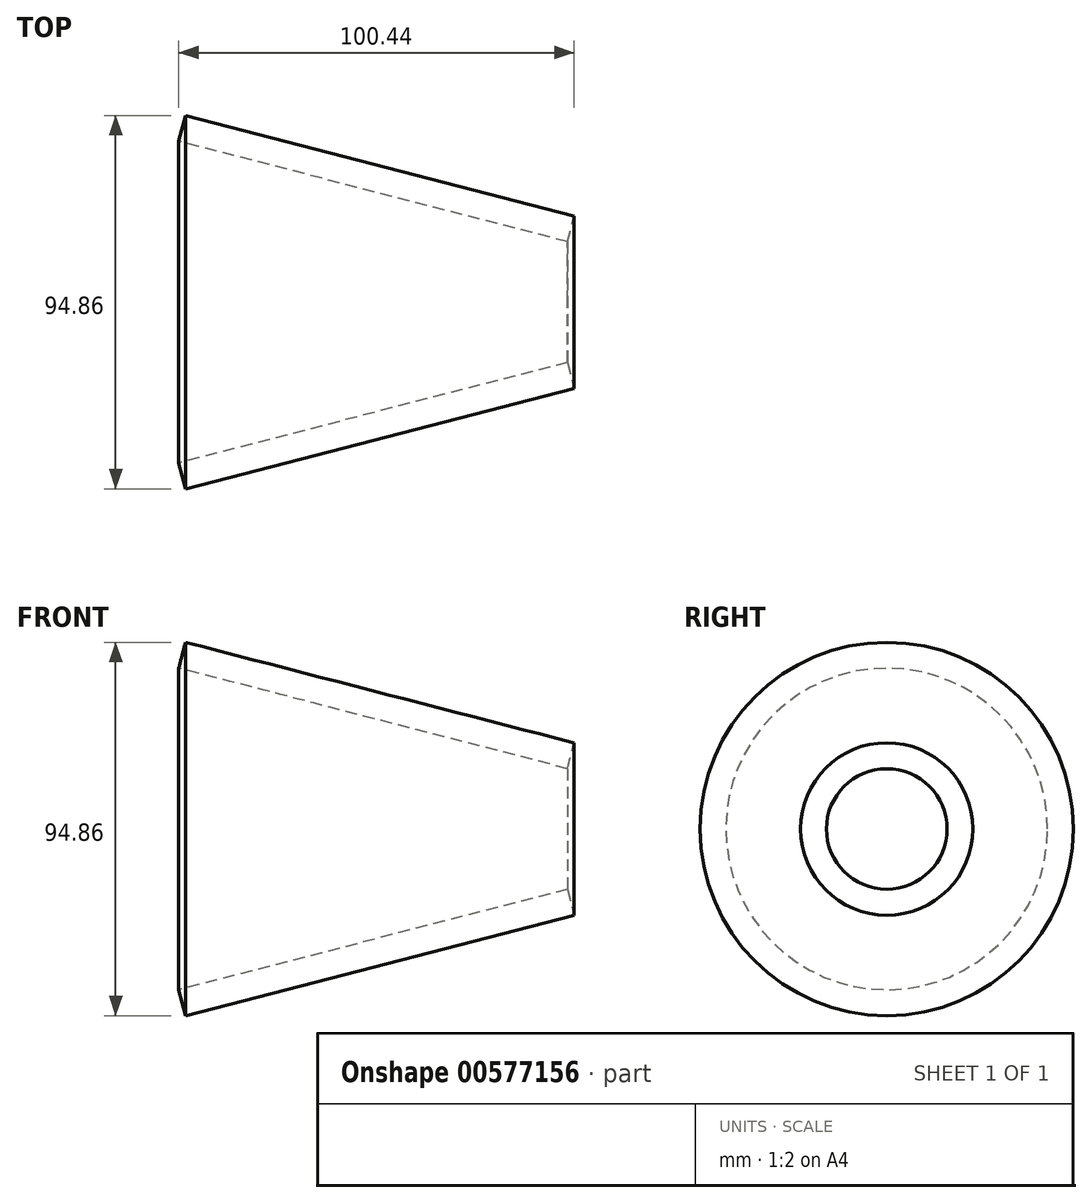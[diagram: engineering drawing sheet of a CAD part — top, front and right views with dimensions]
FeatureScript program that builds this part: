
annotation { "Feature Type Name" : "Feature", "Feature Type Description" : "" }
export const myFeature = defineFeature(function(context is Context, id is Id, definition is map)
    precondition{}
    {
        {
            var Q0;
            Q0=qCreatedBy(makeId("Front.planeOp"),FACE);
            var sketch = newSketch(context, id + "F0", { "sketchPlane" : qUnion([Q0])});
            skLineSegment(sketch, "E0", {"start": v(-38.02, 40.86) * mm, "end": v(60.72, 15.32) * mm});
            skLineSegment(sketch, "E1", {"start": v(-36.6, 0) * mm, "end": v(62.99, 0) * mm});
            skLineSegment(sketch, "E2", {"start": v(-38.02, 40.86) * mm, "end": v(-36.32, 47.43) * mm});
            skLineSegment(sketch, "E3", {"start": v(-36.32, 47.43) * mm, "end": v(62.42, 21.9) * mm});
            skLineSegment(sketch, "E4", {"start": v(60.72, 15.32) * mm, "end": v(62.42, 21.9) * mm});
            skSolve(sketch);
        }
        {
            var Q0;
            Q0 = qSketchRegion(id + "F0", true);
            var Q1;
            Q1=sQuery(id+"F0.wireOp",EDGE,"E1");
            revolve(context, id + "F1", {"entities" : qUnion([Q0]), "axis" : qUnion([Q1]), "revolveType" : RevolveType.FULL});
        }
    });
